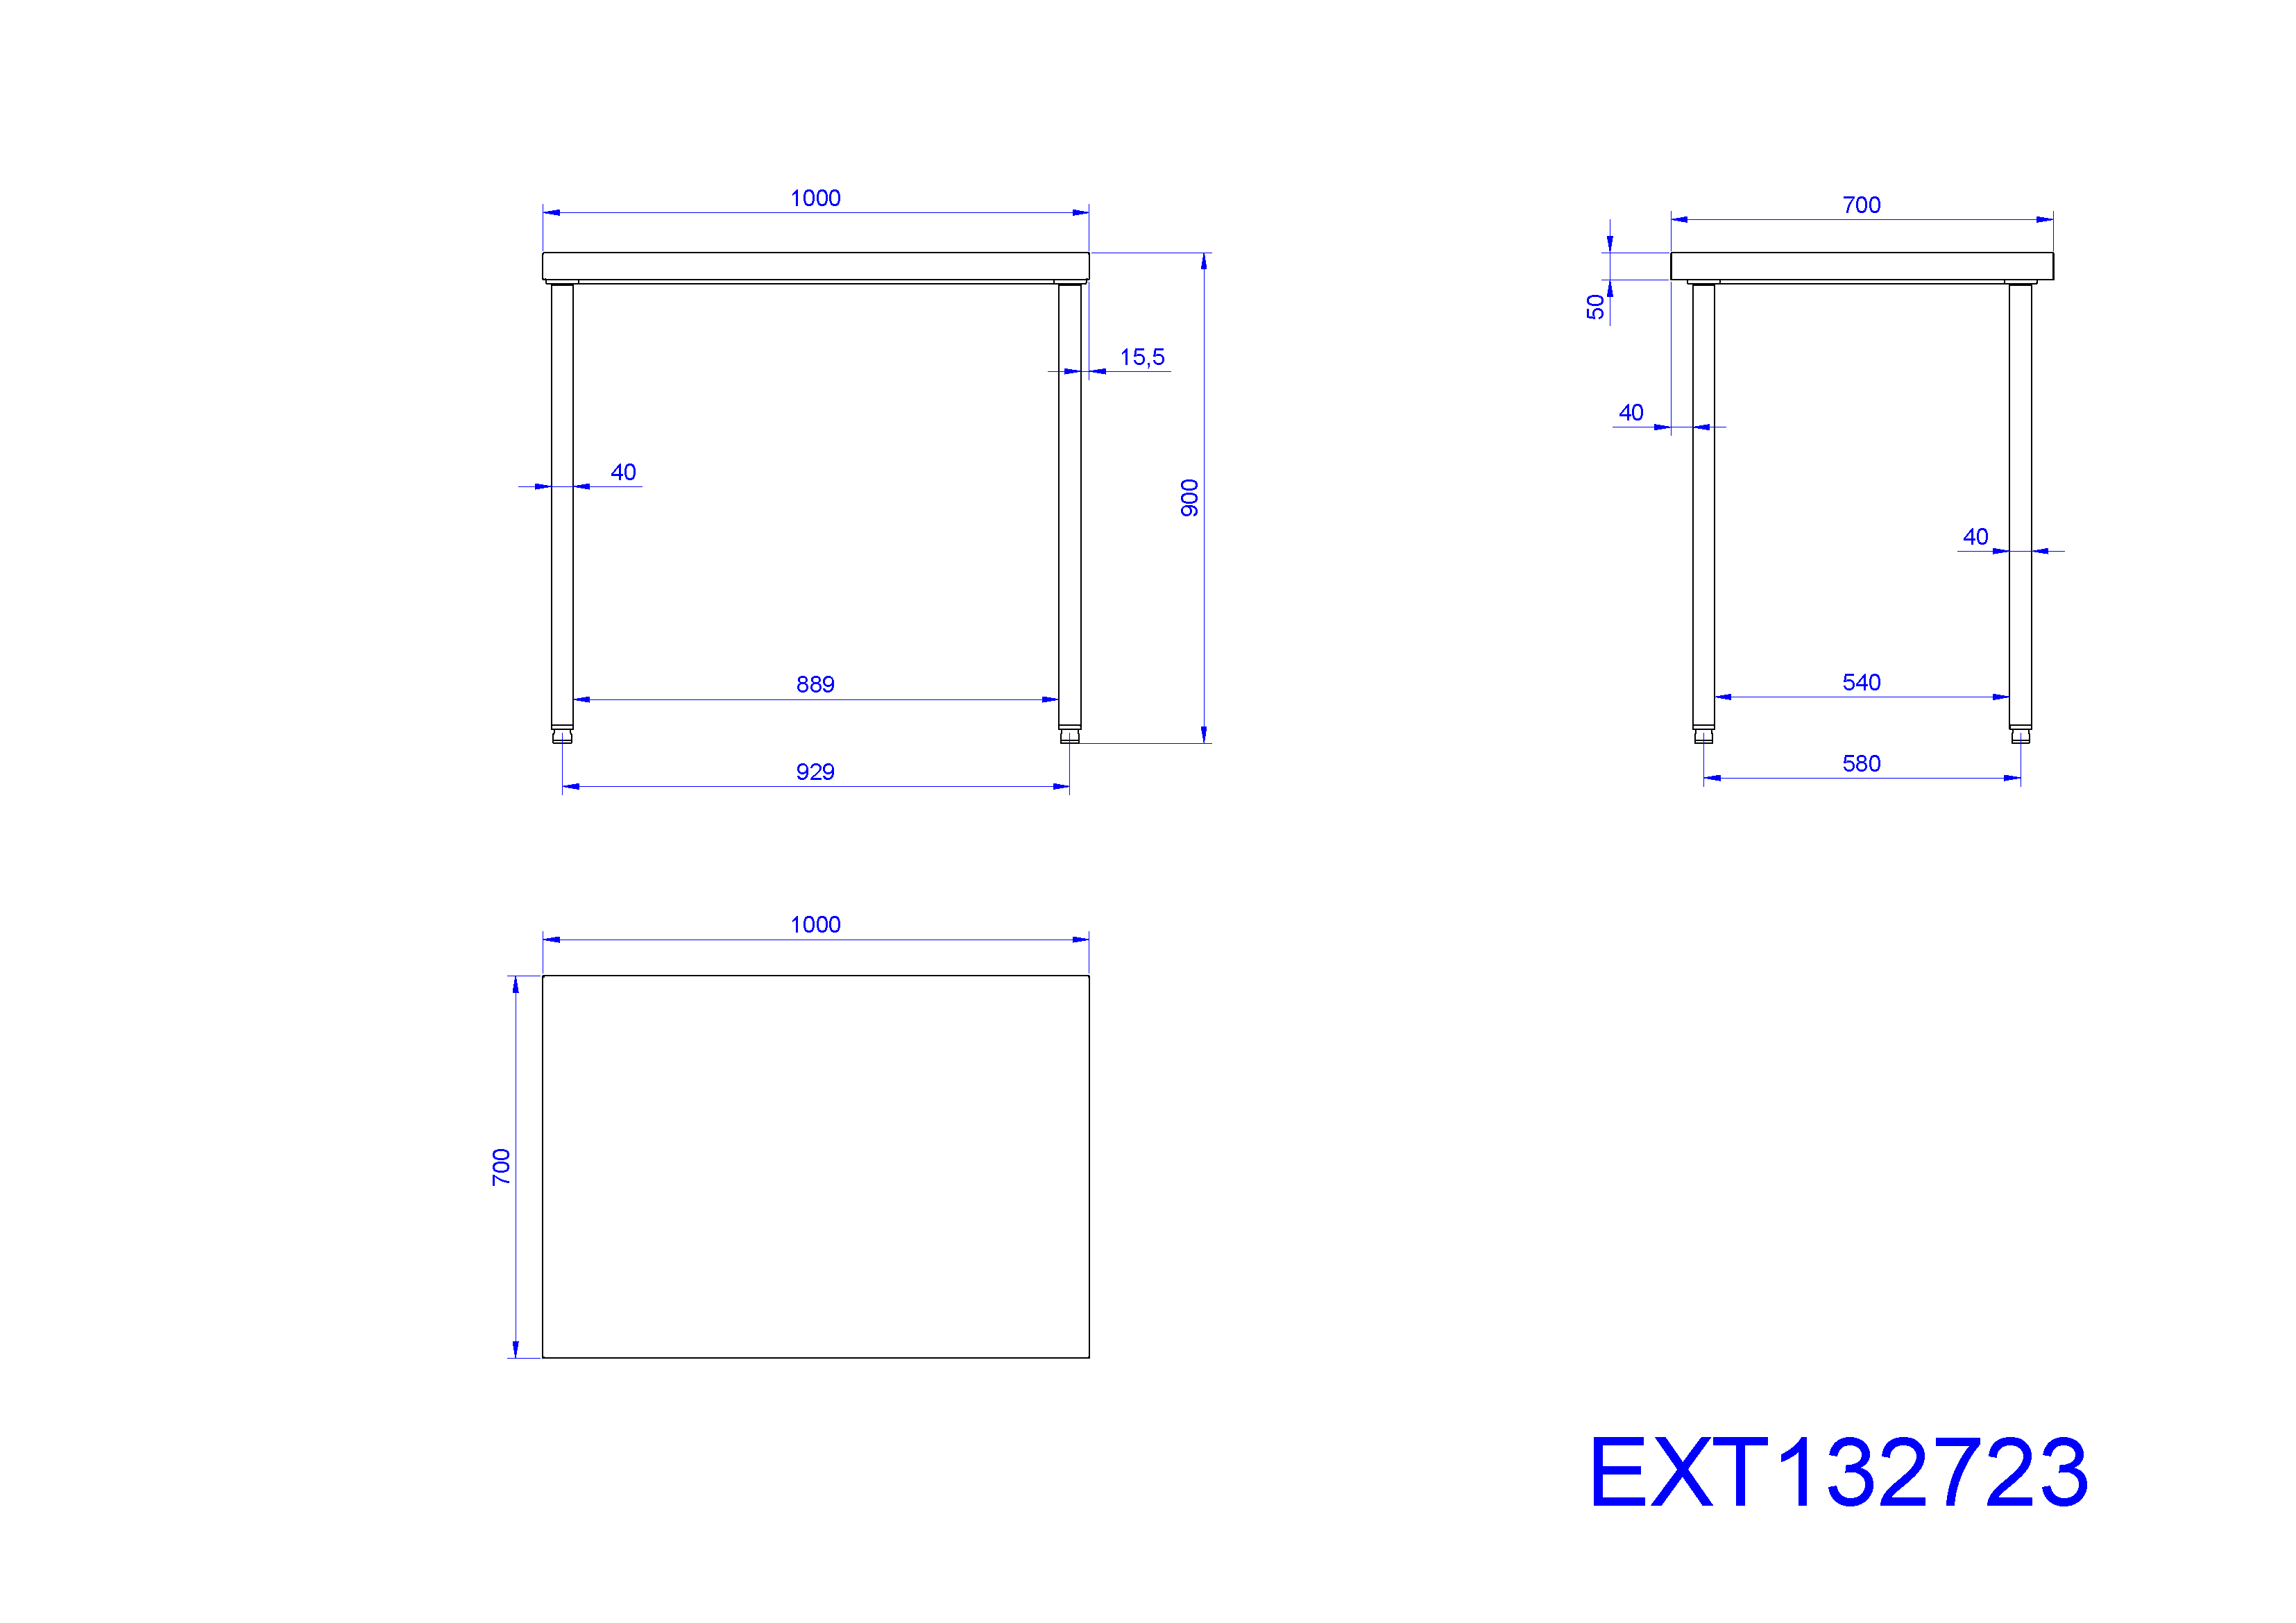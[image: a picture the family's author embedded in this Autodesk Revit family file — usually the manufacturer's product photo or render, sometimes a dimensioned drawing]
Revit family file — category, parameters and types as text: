
# Revit family: QF_ELECTROLUXPROFESSIONAL_132916_ML1S1217RN
name_source: partatom
category: Attrezzature speciali
units: mm (PartAtom-declared; Revit-internal decimal feet)

## family parameters
Basato su piano di lavoro = No
Condiviso = No
Punto di calcolo locali = No
Quota connettore circolare = Usa diametro
Sempre verticale = Sì
Taglio con vuoti quando caricato = No
Tipo di parte = Normale

## types (1)
- Standard
    Accessory = Sì
    Cold Water Size = 0 mm
    Compressed Air Pressure = 0.0 Pa
    Compressed Air Size = 0 mm
    Compressed Air Volume = 0.0 L/s
    Condensate Return Size = 0 mm
    Cycle = 0 Hz
    Depth Actual = 700 mm  [stored 2.29659 ft]
    Descrizione = CUPB.SINK 1 BOWL(500X500)R/H DRAIN. 1200
    Direct Waste Size = 140 mm
    Gas Input Pressure = 0
    Gas KW = 0
    Gas Size = 0 mm
    HP = 0 HP
    Height Actual = 1000 mm  [stored 3.28084 ft]
    Hot Water Size = 0 mm
    Item Number = 132916
    Length Actual = 1200 mm
    Modello = ML1S1217RN
    Phase = 0
    Produttore = Electrolux Professional
    Prospetto di default = 0 mm  [stored 0 ft]
    Refrigerant Compressor Remote = Sì
    Refrigeration Liquid Line Size = 0 mm  [stored 0 ft]
    Refrigeration Suction Line Size = 0 mm  [stored 0 ft]
    Steam Consumption per Hour = 0
    Steam Supply Maximum Pressure = 0.0 Pa
    Steam Supply Minimum Pressure = 0.0 Pa
    Steam Supply Size = 0 mm
    URL = https://www.electroluxprofessional.com
    URL Manufacturer = https://www.electroluxprofessional.com
    Volts = 0 V
    Watts = 0 W
    Weight = 55.00 kg

note: source unit labels omitted for Gas Input Pressure — the stored unit's dimension contradicts the parameter name (converter mislabeling)

note: [stored X ft] marks values corroborated as IEEE doubles in the binary element streams (Revit-internal decimal feet)

## geometry (parser evidence)
native form markers: Sweep x5
no freeform markers — native parametric forms only
